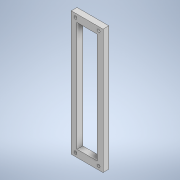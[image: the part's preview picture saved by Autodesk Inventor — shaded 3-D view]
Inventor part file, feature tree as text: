
AUTODESK INVENTOR PART (.ipt)
format: ipt  version: 2020.2 (Build 242310000, 310)  size: 125,440 bytes
history: native  units: mm
features: extrude x1, sketch x1
ambient origin geometry x8: Origin, YZ Plane, XZ Plane, XY Plane, X Axis, Y Axis, Z Axis, Center Point
bodies: Solid1 (feature_tree)
feature tree (2):
  extrude  "Extrusion1"  Depth=86.0mm
  sketch  "Sketch1"  dims[d0=22.0mm d1=86.0mm d2=2.0mm d3=2.0mm d4=2.0mm d5=2.0mm d6=3.0mm d7=2.5mm d8=3.0mm d9=2.5mm d10=2.5mm d11=3.0mm d12=3.0mm d13=2.5mm d14=14.0mm d15=76.0mm d16=4.0mm d17=0.0mm]
